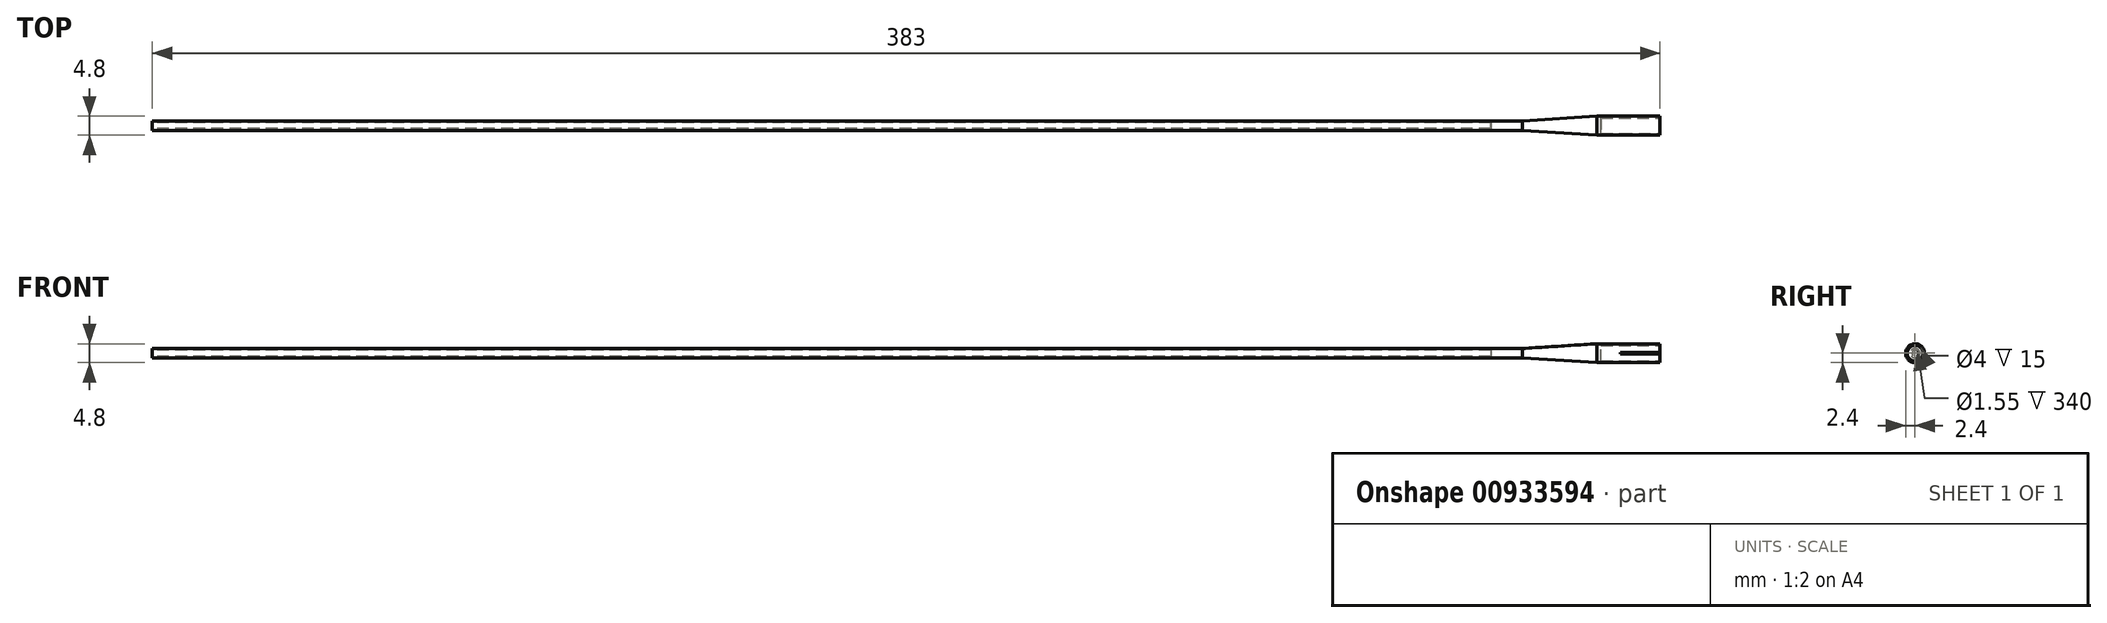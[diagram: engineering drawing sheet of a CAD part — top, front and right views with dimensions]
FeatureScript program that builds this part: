
annotation { "Feature Type Name" : "Feature", "Feature Type Description" : "" }
export const myFeature = defineFeature(function(context is Context, id is Id, definition is map)
    precondition{}
    {
        {
            var Q0;
            Q0=qCreatedBy(makeId("Front.planeOp"),FACE);
            var sketch = newSketch(context, id + "F0", { "sketchPlane" : qUnion([Q0])});
            skLineSegment(sketch, "E0", {"start": v(-23.4, 0) * mm, "end": v(45.68, 0) * mm, "construction": true});
            skLineSegment(sketch, "E1.bottom", {"start": v(26.88, 0) * mm, "end": v(10.88, 0) * mm});
            skLineSegment(sketch, "E1.top", {"start": v(26.88, 2.4) * mm, "end": v(10.88, 2.4) * mm});
            skLineSegment(sketch, "E1.left", {"start": v(26.88, 0) * mm, "end": v(26.88, 2.4) * mm});
            skLineSegment(sketch, "E1.right", {"start": v(10.88, 0) * mm, "end": v(10.88, 2.4) * mm});
            skLineSegment(sketch, "E2", {"start": v(10.88, 0) * mm, "end": v(-8.12, 0) * mm});
            skLineSegment(sketch, "E3", {"start": v(-8.12, 0) * mm, "end": v(-8.12, 1.2) * mm});
            skLineSegment(sketch, "E4", {"start": v(-8.12, 1.2) * mm, "end": v(10.88, 2.4) * mm});
            skLineSegment(sketch, "E5.bottom", {"start": v(-8.12, 0) * mm, "end": v(-356.12, 0) * mm});
            skLineSegment(sketch, "E5.top", {"start": v(-8.12, 1.2) * mm, "end": v(-356.12, 1.2) * mm});
            skLineSegment(sketch, "E5.right", {"start": v(-356.12, 0) * mm, "end": v(-356.12, 1.2) * mm});
            skSolve(sketch);
        }
        {
            var Q0;
            Q0=makeQuery(id+"F0.imprint","IMPRINT",FACE,{"disambiguationData":[TD([[makeQuery(id+"F0.imprint","IMPRINT",EDGE,{"derivedFrom":sQuery(id+"F0.wireOp",EDGE,"E1.bottom")}),-1.0]])]});
            var Q1;
            Q1=makeQuery(id+"F0.imprint","IMPRINT",FACE,{"disambiguationData":[TD([[makeQuery(id+"F0.imprint","IMPRINT",EDGE,{"derivedFrom":sQuery(id+"F0.wireOp",EDGE,"E1.right")}),1.0]])]});
            var Q2;
            Q2=makeQuery(id+"F0.imprint","IMPRINT",FACE,{"disambiguationData":[TD([[makeQuery(id+"F0.imprint","IMPRINT",EDGE,{"derivedFrom":sQuery(id+"F0.wireOp",EDGE,"E5.bottom")}),-1.0]])]});
            var Q3;
            Q3=sQuery(id+"F0.wireOp",EDGE,"E0");
            revolve(context, id + "F1", {"surfaceOperationType" : NewSurfaceOperationType.NEW, "entities" : qUnion([Q0, Q1, Q2]), "axis" : qUnion([Q3]), "revolveType" : RevolveType.FULL});
        }
        {
            var Q0;
            Q0=makeQuery(id+"F1.opRevolve","SWEPT_FACE",FACE,{"disambiguationData":[OSD([sQuery(id+"F0.wireOp",EDGE,"E1.left")])]});
            var sketch = newSketch(context, id + "F2", { "sketchPlane" : qUnion([Q0])});
            skCircle(sketch, "E6", {"center": v(0, 0) * mm, "radius": 2 * mm});
            skSolve(sketch);
        }
        {
            var Q0;
            Q0 = qSketchRegion(id + "F2", true);
            extrude(context, id + "F3", {"entities" : qUnion([Q0]), "operationType" : NewBodyOperationType.REMOVE, "oppositeDirection" : true, "depth" : 15 * mm, "offsetDistance" : 25 * mm});
        }
        {
            var Q0;
            Q0=qCreatedBy(makeId("Front.planeOp"),FACE);
            var sketch = newSketch(context, id + "F4", { "sketchPlane" : qUnion([Q0])});
            skLineSegment(sketch, "E7", {"start": v(0, 0) * mm, "end": v(67.53, 0) * mm, "construction": true});
            skLineSegment(sketch, "E8.bottom", {"start": v(16.88, 0.25) * mm, "end": v(26.88, 0.25) * mm});
            skLineSegment(sketch, "E8.top", {"start": v(16.88, -0.25) * mm, "end": v(26.88, -0.25) * mm});
            skLineSegment(sketch, "E8.left", {"start": v(16.88, 0.25) * mm, "end": v(16.88, -0.25) * mm});
            skLineSegment(sketch, "E8.right", {"start": v(26.88, 0.25) * mm, "end": v(26.88, -0.25) * mm});
            skPoint(sketch, "E8.middle", {"position": v(21.88, 0) * mm});
            skSolve(sketch);
        }
        {
            var Q0;
            Q0 = qSketchRegion(id + "F4", true);
            extrude(context, id + "F5", {"entities" : qUnion([Q0]), "operationType" : NewBodyOperationType.REMOVE, "depth" : 10 * mm, "offsetDistance" : 25 * mm});
        }
        {
            var Q0;
            Q0=makeQuery(id+"F1.opRevolve","SWEPT_FACE",FACE,{"disambiguationData":[OSD([sQuery(id+"F0.wireOp",EDGE,"E5.right")])]});
            var sketch = newSketch(context, id + "F6", { "sketchPlane" : qUnion([Q0])});
            skCircle(sketch, "E9", {"center": v(0, 0) * mm, "radius": 0.78 * mm});
            skSolve(sketch);
        }
        {
            var Q0;
            Q0 = qSketchRegion(id + "F6", true);
            extrude(context, id + "F7", {"entities" : qUnion([Q0]), "operationType" : NewBodyOperationType.REMOVE, "oppositeDirection" : true, "depth" : 340 * mm, "offsetDistance" : 25 * mm});
        }
    });
